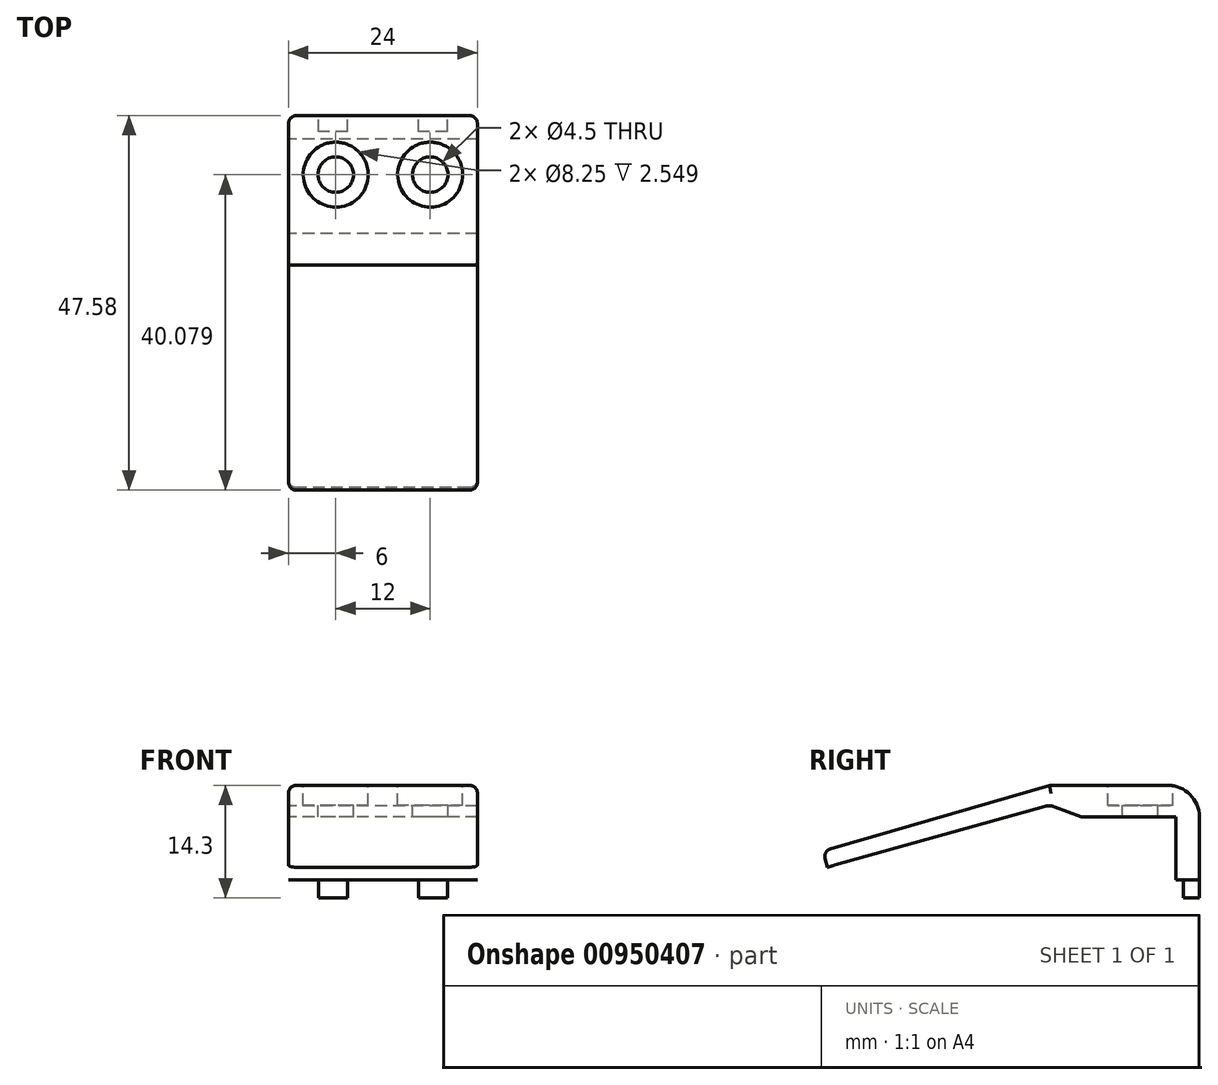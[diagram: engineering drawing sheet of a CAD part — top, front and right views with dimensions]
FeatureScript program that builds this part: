
annotation { "Feature Type Name" : "Feature", "Feature Type Description" : "" }
export const myFeature = defineFeature(function(context is Context, id is Id, definition is map)
    precondition{}
    {
        {
            var Q0;
            Q0=qCreatedBy(makeId("Right.planeOp"),FACE);
            var sketch = newSketch(context, id + "F0", { "sketchPlane" : qUnion([Q0])});
            skLineSegment(sketch, "E0.bottom", {"start": v(-17.95, 8.22) * mm, "end": v(-2.95, 8.22) * mm});
            skLineSegment(sketch, "E0.top", {"start": v(-17.95, 12.22) * mm, "end": v(-6.95, 12.22) * mm});
            skLineSegment(sketch, "E0.left", {"start": v(-17.95, 8.22) * mm, "end": v(-17.95, 12.22) * mm});
            skLineSegment(sketch, "E0.right", {"start": v(-2.95, 8.22) * mm, "end": v(-2.95, 8.22) * mm});
            skLineSegment(sketch, "E1.bottom", {"start": v(-2.95, 8.22) * mm, "end": v(-5.95, 8.22) * mm});
            skLineSegment(sketch, "E1.top", {"start": v(-2.95, 0.22) * mm, "end": v(-5.95, 0.22) * mm});
            skLineSegment(sketch, "E1.left", {"start": v(-2.95, 8.22) * mm, "end": v(-2.95, 0.22) * mm});
            skLineSegment(sketch, "E1.right", {"start": v(-5.95, 8.22) * mm, "end": v(-5.95, 0.22) * mm});
            skPoint(sketch, "E2.visualSharp", {"position": v(-2.95, 12.22) * mm});
            skArc(sketch, "E2.filletArc", {"start": v(-2.95, 8.22) * mm, "mid": v(-4.12, 11.05) * mm, "end": v(-6.95, 12.22) * mm});
            skLineSegment(sketch, "E3", {"start": v(-17.95, 12.22) * mm, "end": v(-21.95, 12.22) * mm});
            skLineSegment(sketch, "E4", {"start": v(-21.95, 12.22) * mm, "end": v(-21.95, 9.72) * mm});
            skLineSegment(sketch, "E5", {"start": v(-21.34, 9.49) * mm, "end": v(-17.95, 8.22) * mm});
            skLineSegment(sketch, "E6", {"start": v(-21.95, 12.22) * mm, "end": v(-49.8, 4.15) * mm});
            skLineSegment(sketch, "E7", {"start": v(-50.49, 2.9) * mm, "end": v(-50.17, 1.81) * mm});
            skLineSegment(sketch, "E8", {"start": v(-50.17, 1.81) * mm, "end": v(-22.58, 9.54) * mm});
            skPoint(sketch, "E9.visualSharp", {"position": v(-21.95, 9.72) * mm});
            skArc(sketch, "E9.filletArc", {"start": v(-21.34, 9.49) * mm, "mid": v(-21.96, 9.61) * mm, "end": v(-22.58, 9.54) * mm});
            skPoint(sketch, "E10.visualSharp", {"position": v(-50.77, 3.87) * mm});
            skArc(sketch, "E10.filletArc", {"start": v(-49.8, 4.15) * mm, "mid": v(-50.4, 3.67) * mm, "end": v(-50.49, 2.9) * mm});
            skSolve(sketch);
        }
        {
            var Q0;
            Q0=makeQuery(id+"F0.imprint","IMPRINT",FACE,{"disambiguationData":[TD([[makeQuery(id+"F0.imprint","IMPRINT",EDGE,{"derivedFrom":sQuery(id+"F0.wireOp",EDGE,"E0.left")}),1.0]])]});
            var Q1;
            Q1=makeQuery(id+"F0.imprint","IMPRINT",FACE,{"disambiguationData":[TD([[makeQuery(id+"F0.imprint","IMPRINT",EDGE,{"derivedFrom":sQuery(id+"F0.wireOp",EDGE,"E0.bottom")}),1.0]])]});
            var Q2;
            Q2=makeQuery(id+"F0.imprint","IMPRINT",FACE,{"disambiguationData":[TD([[makeQuery(id+"F0.imprint","IMPRINT",EDGE,{"derivedFrom":sQuery(id+"F0.wireOp",EDGE,"E1.bottom")}),1.0]])]});
            var Q3;
            Q3 = qSketchRegion(id + "F0", true);
            extrude(context, id + "F1", {"entities" : qUnion([Q0, Q1, Q2, Q3]), "depth" : 24 * mm, "offsetDistance" : 25 * mm});
        }
        {
            var Q0;
            Q0=makeQuery(id+"F1.opExtrude","SWEPT_FACE",FACE,{"disambiguationData":[OSD([sQuery(id+"F0.wireOp",EDGE,"E0.top"),sQuery(id+"F0.wireOp",EDGE,"E3")])]});
            var sketch = newSketch(context, id + "F2", { "sketchPlane" : qUnion([Q0])});
            skLineSegment(sketch, "E11", {"start": v(12, -6.95) * mm, "end": v(12, -21.95) * mm});
            skLineSegment(sketch, "E12", {"start": v(0, -10.45) * mm, "end": v(12, -10.45) * mm});
            skLineSegment(sketch, "E13", {"start": v(12, -10.45) * mm, "end": v(24, -10.45) * mm});
            skPoint(sketch, "E14", {"position": v(6, -10.45) * mm});
            skPoint(sketch, "E15", {"position": v(18, -10.45) * mm});
            skSolve(sketch);
        }
        {
            var Q0;
            Q0=sQuery(id+"F2.wireOp",VERTEX,"E14");
            var Q1;
            Q1=sQuery(id+"F2.wireOp",VERTEX,"E15");
            var Q2;
            Q2=makeQuery(id+"F1.opExtrude","SWEPT_BODY",BODY,{"disambiguationData":[OSD([sQuery(id+"F0.wireOp",EDGE,"E0.bottom"),sQuery(id+"F0.wireOp",EDGE,"E0.top"),sQuery(id+"F0.wireOp",EDGE,"E1.top"),sQuery(id+"F0.wireOp",EDGE,"E1.left"),sQuery(id+"F0.wireOp",EDGE,"E1.right"),sQuery(id+"F0.wireOp",EDGE,"E2.filletArc"),sQuery(id+"F0.wireOp",EDGE,"E3"),sQuery(id+"F0.wireOp",EDGE,"E5"),sQuery(id+"F0.wireOp",EDGE,"E6"),sQuery(id+"F0.wireOp",EDGE,"E7"),sQuery(id+"F0.wireOp",EDGE,"E8"),sQuery(id+"F0.wireOp",EDGE,"E9.filletArc"),sQuery(id+"F0.wireOp",EDGE,"E10.filletArc")])]});
            hole(context, id + "F3", {"style" : HoleStyle.C_BORE, "endStyle" : HoleEndStyle.THROUGH, "holeDiameter" : 4.5 * mm, "cBoreDiameter" : 8.25 * mm, "cBoreDepth" : 2.5 * mm, "majorDiameter" : 5 * mm, "isTappedThrough" : true, "tappedDepth" : 12 * mm, "tapClearance" : 3, "locations" : qUnion([Q0, Q1]), "scope" : qUnion([Q2])});
        }
        {
            var Q0;
            Q0=makeQuery(id+"F1.opExtrude","CAP_EDGE",EDGE,{"disambiguationData":[OSD([sQuery(id+"F0.wireOp",EDGE,"E6")])],"isStart":false});
            var Q1;
            Q1=makeQuery(id+"F1.opExtrude","CAP_EDGE",EDGE,{"disambiguationData":[OSD([sQuery(id+"F0.wireOp",EDGE,"E6")])],"isStart":true});
            var Q2;
            Q2=makeQuery(id+"F1.opExtrude","CAP_EDGE",EDGE,{"disambiguationData":[OSD([sQuery(id+"F0.wireOp",EDGE,"E0.top"),sQuery(id+"F0.wireOp",EDGE,"E3")])],"isStart":false});
            var Q3;
            Q3=makeQuery(id+"F1.opExtrude","CAP_EDGE",EDGE,{"disambiguationData":[OSD([sQuery(id+"F0.wireOp",EDGE,"E0.top"),sQuery(id+"F0.wireOp",EDGE,"E3")])],"isStart":true});
            fillet(context, id + "F4", {"entities" : qUnion([Q0, Q1, Q2, Q3]), "radius" : 1 * mm, "tangentPropagation" : true, "allowEdgeOverflow" : false});
        }
        {
            var Q0;
            Q0=makeQuery(id+"F1.opExtrude","SWEPT_FACE",FACE,{"disambiguationData":[OSD([sQuery(id+"F0.wireOp",EDGE,"E1.left")])]});
            var sketch = newSketch(context, id + "F5", { "sketchPlane" : qUnion([Q0])});
            skLineSegment(sketch, "E16.bottom", {"start": v(-20.2, 0.22) * mm, "end": v(-16.5, 0.22) * mm});
            skLineSegment(sketch, "E16.top", {"start": v(-20.2, -2.08) * mm, "end": v(-16.5, -2.08) * mm});
            skLineSegment(sketch, "E16.left", {"start": v(-20.2, 0.22) * mm, "end": v(-20.2, -2.08) * mm});
            skLineSegment(sketch, "E16.right", {"start": v(-16.5, 0.22) * mm, "end": v(-16.5, -2.08) * mm});
            skLineSegment(sketch, "E17", {"start": v(-12, 0.22) * mm, "end": v(-16.5, 0.22) * mm});
            skLineSegment(sketch, "E18.bottom", {"start": v(-7.5, 0.22) * mm, "end": v(-3.8, 0.22) * mm});
            skLineSegment(sketch, "E18.top", {"start": v(-7.5, -2.08) * mm, "end": v(-3.8, -2.08) * mm});
            skLineSegment(sketch, "E18.left", {"start": v(-7.5, 0.22) * mm, "end": v(-7.5, -2.08) * mm});
            skLineSegment(sketch, "E18.right", {"start": v(-3.8, 0.22) * mm, "end": v(-3.8, -2.08) * mm});
            skLineSegment(sketch, "E19", {"start": v(-12, 0.22) * mm, "end": v(-7.5, 0.22) * mm});
            skSolve(sketch);
        }
        {
            var Q0;
            Q0 = qSketchRegion(id + "F5", true);
            extrude(context, id + "F6", {"entities" : qUnion([Q0]), "oppositeDirection" : true, "depth" : 2 * mm, "offsetDistance" : 25 * mm});
        }
    });
